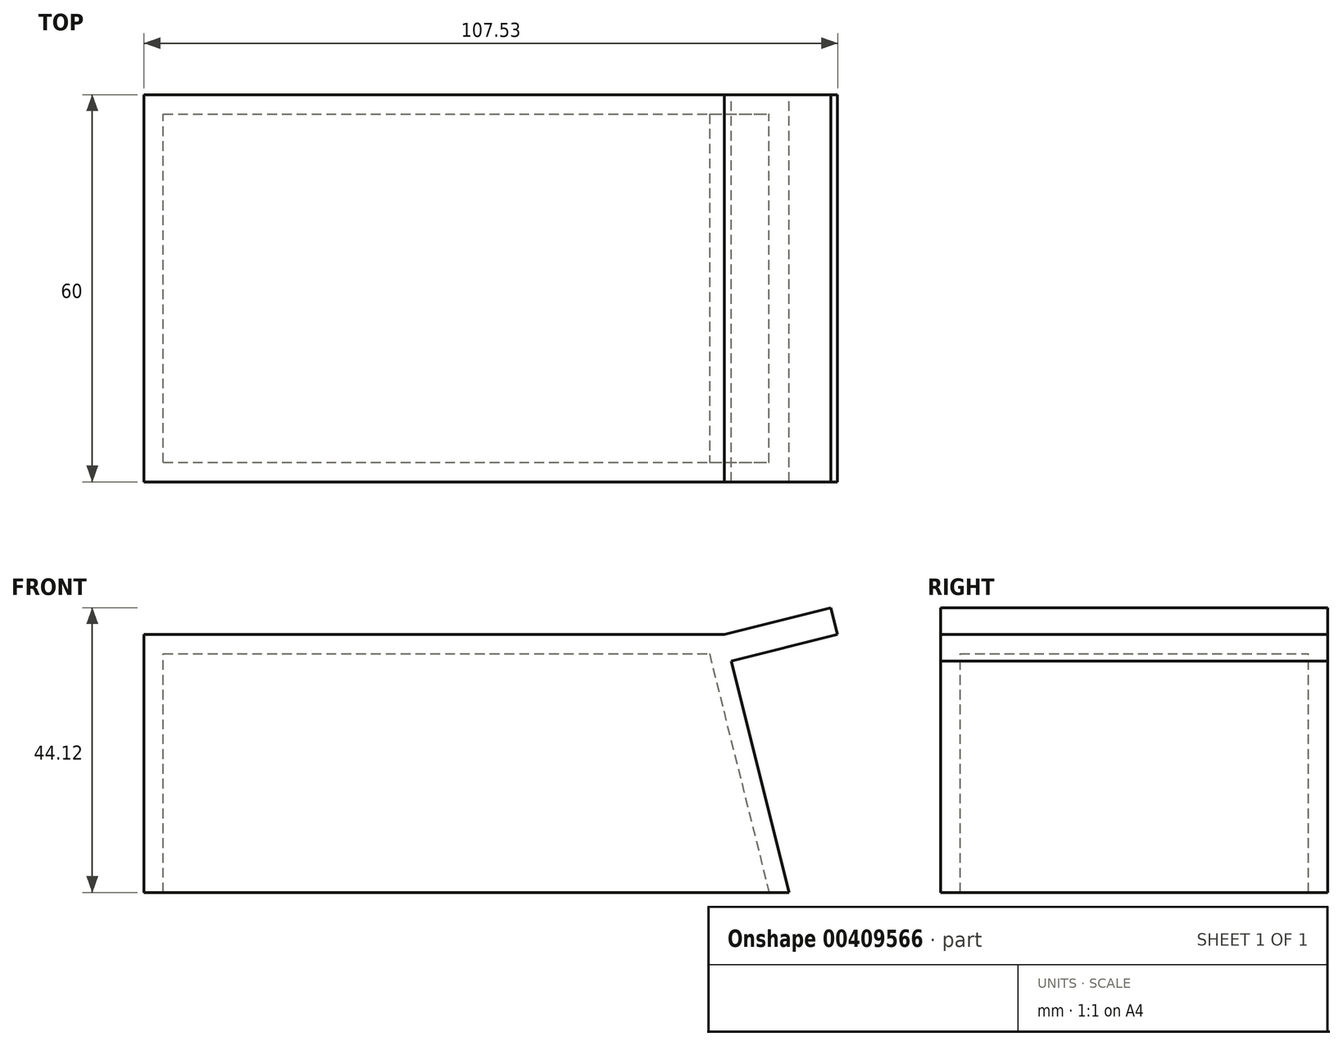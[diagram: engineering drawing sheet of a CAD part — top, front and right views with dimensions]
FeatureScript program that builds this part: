
annotation { "Feature Type Name" : "Feature", "Feature Type Description" : "" }
export const myFeature = defineFeature(function(context is Context, id is Id, definition is map)
    precondition{}
    {
        {
            var Q0;
            Q0=qCreatedBy(makeId("Front.planeOp"),FACE);
            var sketch = newSketch(context, id + "F0", { "sketchPlane" : qUnion([Q0])});
            skLineSegment(sketch, "E0", {"start": v(-57.2, 0) * mm, "end": v(42.8, 0) * mm});
            skLineSegment(sketch, "E1", {"start": v(-57.2, 0) * mm, "end": v(-57.2, 40) * mm});
            skLineSegment(sketch, "E2", {"start": v(-57.2, 40) * mm, "end": v(32.8, 40) * mm});
            skLineSegment(sketch, "E3", {"start": v(32.8, 40) * mm, "end": v(42.8, 0) * mm});
            skLineSegment(sketch, "E4", {"start": v(32.8, 40) * mm, "end": v(49.3, 44.12) * mm});
            skLineSegment(sketch, "E5", {"start": v(49.3, 44.12) * mm, "end": v(50.33, 40) * mm});
            skLineSegment(sketch, "E6", {"start": v(50.33, 40) * mm, "end": v(33.83, 35.88) * mm});
            skSolve(sketch);
        }
        {
            var Q0;
            Q0=makeQuery(id+"F0.imprint","IMPRINT",FACE,{"disambiguationData":[TD([[makeQuery(id+"F0.imprint","IMPRINT",EDGE,{"derivedFrom":sQuery(id+"F0.wireOp",EDGE,"E0")}),1.0]])]});
            extrude(context, id + "F1", {"entities" : qUnion([Q0]), "depth" : 60 * mm});
        }
        {
            var Q0;
            {var subQ0=sQuery(id+"F0.wireOp",EDGE,"E4");Q0=makeQuery(id+"F0.imprint","IMPRINT",FACE,{"disambiguationData":[TD([[makeQuery(id+"F0.imprint","IMPRINT",EDGE,{"derivedFrom":subQ0}),-1.0]])]});}
            extrude(context, id + "F2", {"entities" : qUnion([Q0]), "operationType" : NewBodyOperationType.ADD, "depth" : 60 * mm});
        }
        {
            var Q0;
            Q0=makeQuery(id+"F1.opExtrude","SWEPT_FACE",FACE,{"disambiguationData":[OSD([sQuery(id+"F0.wireOp",EDGE,"E0")])]});
            shell(context, id + "F3", {"entities" : qUnion([Q0]), "thickness" : 3 * mm});
        }
    });
